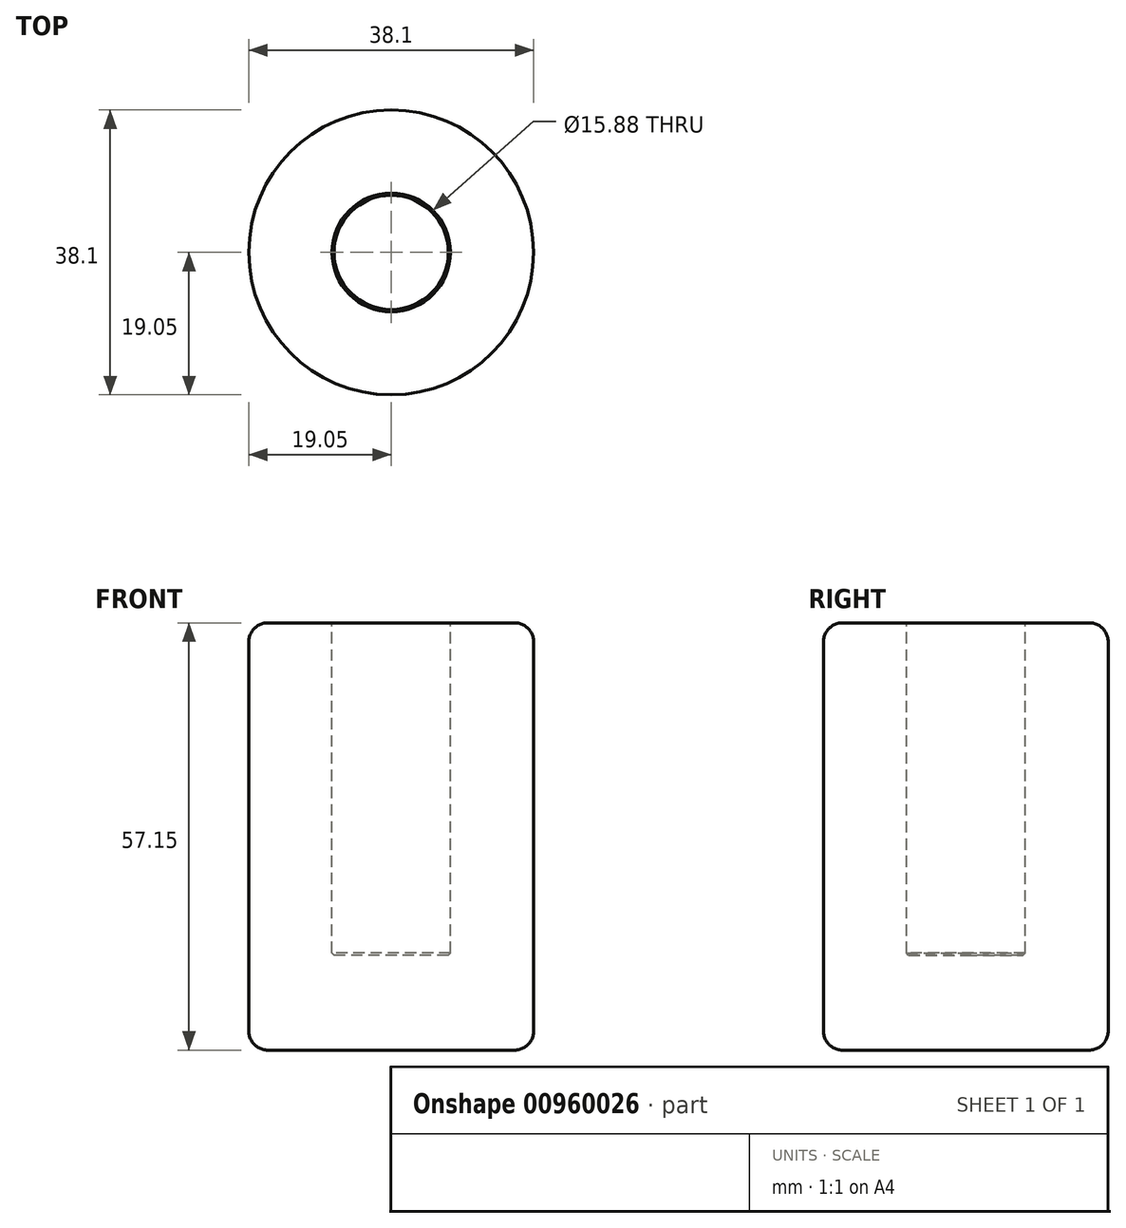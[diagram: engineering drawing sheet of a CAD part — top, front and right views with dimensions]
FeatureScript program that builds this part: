
annotation { "Feature Type Name" : "Feature", "Feature Type Description" : "" }
export const myFeature = defineFeature(function(context is Context, id is Id, definition is map)
    precondition{}
    {
        {
            var Q0;
            Q0=qCreatedBy(makeId("Top.planeOp"),FACE);
            var sketch = newSketch(context, id + "F0", { "sketchPlane" : qUnion([Q0])});
            skCircle(sketch, "E0", {"center": v(0, 0) * mm, "radius": 19.05 * mm});
            skSolve(sketch);
        }
        {
            var Q0;
            Q0=qSketchRegion(id+"F0",true);
            extrude(context, id + "F1", {"entities" : qUnion([Q0]), "depth" : 57.15 * mm, "offsetDistance" : 25.4 * mm});
        }
        {
            var Q0;
            Q0=makeQuery(id+"F1.opExtrude","CAP_FACE",FACE,{"disambiguationData":[OSD([sQuery(id+"F0.wireOp",EDGE,"E0")])],"isStart":false});
            var sketch = newSketch(context, id + "F2", { "sketchPlane" : qUnion([Q0])});
            skCircle(sketch, "E1", {"center": v(0, 0) * mm, "radius": 7.94 * mm});
            skSolve(sketch);
        }
        {
            var Q0;
            Q0=qSketchRegion(id+"F2",true);
            extrude(context, id + "F3", {"entities" : qUnion([Q0]), "operationType" : NewBodyOperationType.REMOVE, "oppositeDirection" : true, "depth" : 44.45 * mm, "offsetDistance" : 25.4 * mm});
        }
        {
            var Q0;
            Q0=makeQuery(id+"F1.opExtrude","CAP_FACE",FACE,{"disambiguationData":[OSD([sQuery(id+"F0.wireOp",EDGE,"E0")])],"isStart":true});
            var Q1;
            Q1=makeQuery(id+"F1.opExtrude","CAP_EDGE",EDGE,{"disambiguationData":[OSD([sQuery(id+"F0.wireOp",EDGE,"E0")])],"isStart":false});
            fillet(context, id + "F4", {"entities" : qUnion([Q0, Q1]), "radius" : 2.54 * mm, "tangentPropagation" : true, "allowEdgeOverflow" : false});
        }
        {
            var Q0;
            Q0=makeQuery(id+"F3.boolean.opBoolean","COPY",EDGE,{"derivedFrom":makeQuery(id+"F3.opExtrude","CAP_EDGE",EDGE,{"disambiguationData":[OSD([sQuery(id+"F2.wireOp",EDGE,"E1")])],"isStart":true})});
            var Q1;
            Q1=makeQuery(id+"F3.boolean.opBoolean","COPY",EDGE,{"derivedFrom":makeQuery(id+"F3.opExtrude","CAP_EDGE",EDGE,{"disambiguationData":[OSD([sQuery(id+"F2.wireOp",EDGE,"E1")])],"isStart":false})});
            chamfer(context, id + "F5", {"entities" : qUnion([Q0, Q1]), "width" : .3 * mm, "tangentPropagation" : true});
        }
    });
